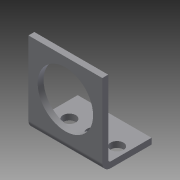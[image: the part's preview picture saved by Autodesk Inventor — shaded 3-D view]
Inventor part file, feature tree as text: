
AUTODESK INVENTOR PART (.ipt)
format: ipt  version: 2013 (Build 170138000, 138)  size: 128,512 bytes
history: native  units: in
note: dims shown in document units (in); Inventor stores cm internally (conversion verified against a paired STEP export)
features: sketch x5, other x5, sheet_metal_op x4, reference x3
ambient origin geometry x8: Origin, YZ Plane, XZ Plane, XY Plane, X Axis, Y Axis, Z Axis, Center Point
bodies: Solid1 (feature_tree)
feature tree (17):
  sheet_metal_op  "Face1"
  sheet_metal_op  "Flange1"
  sketch  "Sketch1"  dims[d0=1.5in]
  other  "Plate1"
  sketch  "Sketch2"  dims[d1=1.5in]
  sketch  "Sketch3"  dims[d2=0.75in]
  other  "Plate2"
  sheet_metal_op  "Bend1"
  sheet_metal_op  "Corner1"
  sketch  "Sketch6"  dims[d3=0.75in]
  reference  "Reference1"
  reference  "Reference2"
  sketch  "Sketch7"  dims[d4=0.12in d7=0.75in d8=1.125in d9=0.12in d10=0.0in d11=0.12in d12=0.06in d13=0.24in d14=0.12in d15=1.0in d16=90.0deg d17=0.05in d18=0.48in d19=0.12in d20=0.12in d28=0.12in d29=0.0in d30=0.12in d31=0.0in]
  reference  "Reference3"
  other  "Cut1"
  other  "Cut3"
  other  "Cut4"
